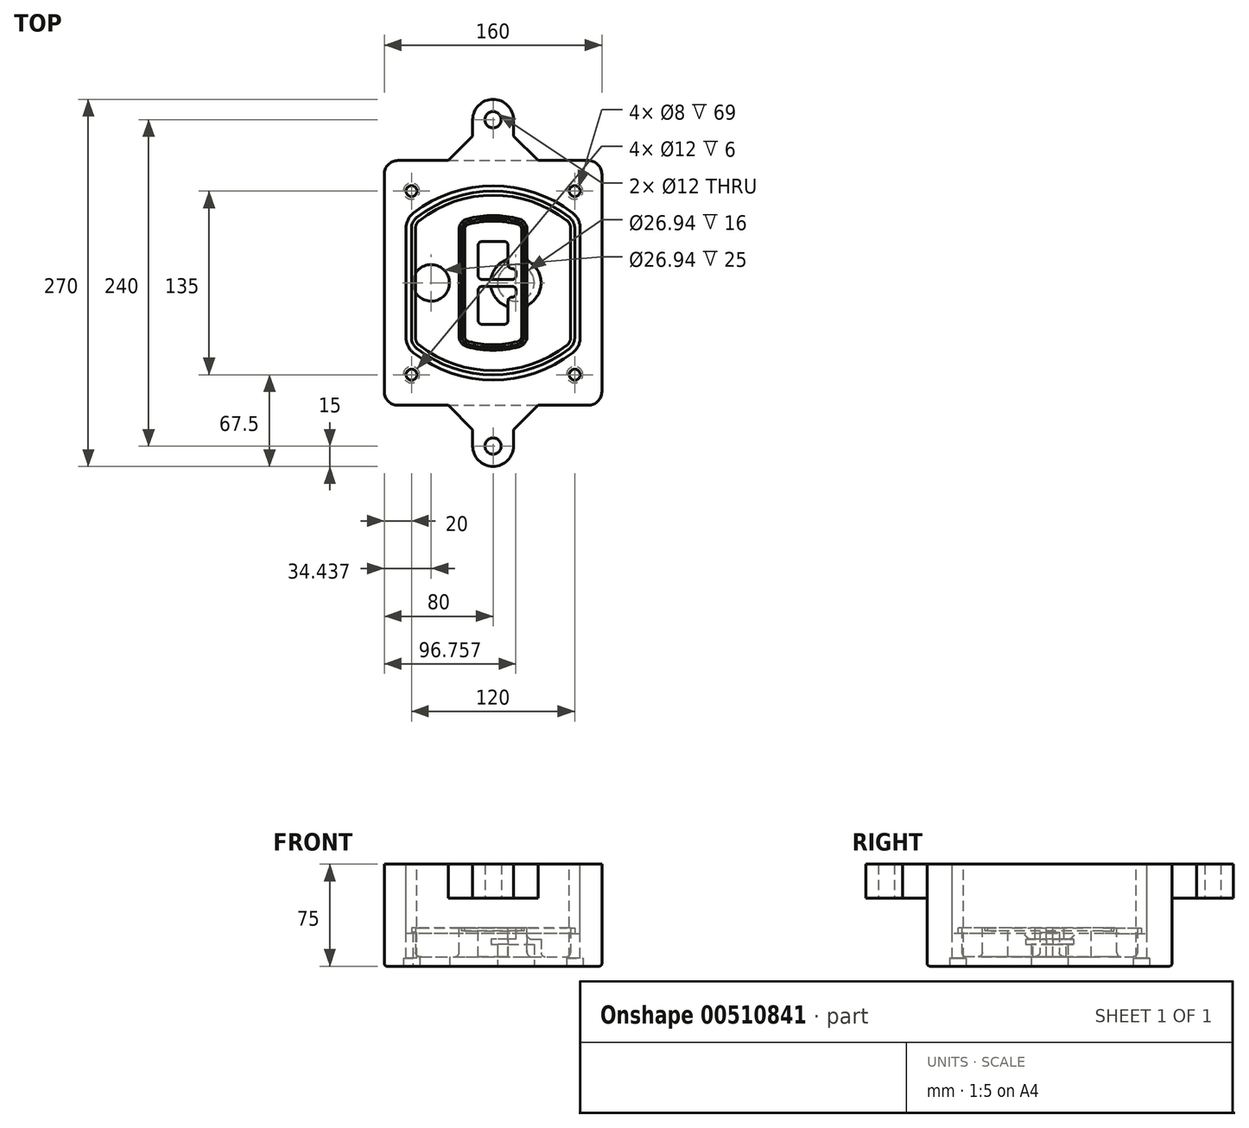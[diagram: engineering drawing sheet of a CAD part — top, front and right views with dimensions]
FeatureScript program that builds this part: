
annotation { "Feature Type Name" : "Feature", "Feature Type Description" : "" }
export const myFeature = defineFeature(function(context is Context, id is Id, definition is map)
    precondition{}
    {
        {
            var Q0;
            Q0=qCreatedBy(makeId("Top.planeOp"),FACE);
            var sketch = newSketch(context, id + "F0", { "sketchPlane" : qUnion([Q0])});
            skPoint(sketch, "E0.rect.middle", {"position": v(0, 0) * mm});
            skLineSegment(sketch, "E1.bottom", {"start": v(-70, -90) * mm, "end": v(70, -90) * mm});
            skLineSegment(sketch, "E1.top", {"start": v(-70, 90) * mm, "end": v(70, 90) * mm});
            skLineSegment(sketch, "E1.left", {"start": v(-80, -80) * mm, "end": v(-80, 80) * mm});
            skLineSegment(sketch, "E1.right", {"start": v(80, -80) * mm, "end": v(80, 80) * mm});
            skLineSegment(sketch, "E2", {"start": v(-80, 90) * mm, "end": v(80, -90) * mm, "construction": true});
            skLineSegment(sketch, "E3", {"start": v(80, 90) * mm, "end": v(-80, -90) * mm, "construction": true});
            skCircle(sketch, "E4", {"center": v(-60, 67.5) * mm, "radius": 4 * mm});
            skCircle(sketch, "E5", {"center": v(60, 67.5) * mm, "radius": 4 * mm});
            skCircle(sketch, "E6", {"center": v(60, -67.5) * mm, "radius": 4 * mm});
            skCircle(sketch, "E7", {"center": v(-60, -67.5) * mm, "radius": 4 * mm});
            skLineSegment(sketch, "E8", {"start": v(-60, 67.5) * mm, "end": v(60, 67.5) * mm, "construction": true});
            skLineSegment(sketch, "E9", {"start": v(60, 67.5) * mm, "end": v(60, -67.5) * mm, "construction": true});
            skLineSegment(sketch, "E10", {"start": v(60, -67.5) * mm, "end": v(-60, -67.5) * mm, "construction": true});
            skLineSegment(sketch, "E11", {"start": v(-60, -67.5) * mm, "end": v(-60, 67.5) * mm, "construction": true});
            skLineSegment(sketch, "E12", {"start": v(-60, 40.3) * mm, "end": v(-60, -40.3) * mm});
            skLineSegment(sketch, "E13", {"start": v(60, 40.3) * mm, "end": v(60, -40.3) * mm});
            skArc(sketch, "E14", {"start": v(56.15, 48.18) * mm, "mid": v(0, 67.5) * mm, "end": v(-56.15, 48.18) * mm});
            skArc(sketch, "E15", {"start": v(-56.15, -48.18) * mm, "mid": v(0, -67.5) * mm, "end": v(56.15, -48.18) * mm});
            skLineSegment(sketch, "E16", {"start": v(-60, 0) * mm, "end": v(60, 0) * mm, "construction": true});
            skPoint(sketch, "E17.visualSharp", {"position": v(-60, -45) * mm});
            skArc(sketch, "E17.filletArc", {"start": v(-60, -40.3) * mm, "mid": v(-58.99, -44.68) * mm, "end": v(-56.15, -48.18) * mm});
            skPoint(sketch, "E18.visualSharp", {"position": v(-60, 45) * mm});
            skArc(sketch, "E18.filletArc", {"start": v(-56.15, 48.18) * mm, "mid": v(-58.99, 44.68) * mm, "end": v(-60, 40.3) * mm});
            skPoint(sketch, "E19.visualSharp", {"position": v(60, 45) * mm});
            skArc(sketch, "E19.filletArc", {"start": v(60, 40.3) * mm, "mid": v(58.99, 44.68) * mm, "end": v(56.15, 48.18) * mm});
            skPoint(sketch, "E20.visualSharp", {"position": v(60, -45) * mm});
            skArc(sketch, "E20.filletArc", {"start": v(56.15, -48.18) * mm, "mid": v(58.99, -44.68) * mm, "end": v(60, -40.3) * mm});
            skPoint(sketch, "E21.visualSharp", {"position": v(-80, 90) * mm});
            skArc(sketch, "E21.filletArc", {"start": v(-70, 90) * mm, "mid": v(-77.07, 87.07) * mm, "end": v(-80, 80) * mm});
            skPoint(sketch, "E22.visualSharp", {"position": v(80, 90) * mm});
            skArc(sketch, "E22.filletArc", {"start": v(80, 80) * mm, "mid": v(77.07, 87.07) * mm, "end": v(70, 90) * mm});
            skPoint(sketch, "E23.visualSharp", {"position": v(80, -90) * mm});
            skArc(sketch, "E23.filletArc", {"start": v(70, -90) * mm, "mid": v(77.07, -87.07) * mm, "end": v(80, -80) * mm});
            skPoint(sketch, "E24.visualSharp", {"position": v(-80, -90) * mm});
            skArc(sketch, "E24.filletArc", {"start": v(-80, -80) * mm, "mid": v(-77.07, -87.07) * mm, "end": v(-70, -90) * mm});
            skArc(sketch, "E25.0", {"start": v(57, 40.3) * mm, "mid": v(56.3, 43.36) * mm, "end": v(54.3, 45.81) * mm});
            skLineSegment(sketch, "E25.1", {"start": v(57, 40.3) * mm, "end": v(57, -40.3) * mm});
            skArc(sketch, "E25.2", {"start": v(54.3, -45.81) * mm, "mid": v(56.3, -43.36) * mm, "end": v(57, -40.3) * mm});
            skArc(sketch, "E25.3", {"start": v(-54.3, -45.81) * mm, "mid": v(0, -64.5) * mm, "end": v(54.3, -45.81) * mm});
            skArc(sketch, "E25.4", {"start": v(-57, -40.3) * mm, "mid": v(-56.3, -43.36) * mm, "end": v(-54.3, -45.81) * mm});
            skArc(sketch, "E25.5", {"start": v(54.3, 45.81) * mm, "mid": v(0, 64.5) * mm, "end": v(-54.3, 45.81) * mm});
            skLineSegment(sketch, "E25.6", {"start": v(-57, 40.3) * mm, "end": v(-57, -40.3) * mm});
            skArc(sketch, "E25.7", {"start": v(-54.3, 45.81) * mm, "mid": v(-56.3, 43.36) * mm, "end": v(-57, 40.3) * mm});
            skArc(sketch, "E26.0", {"start": v(-58.62, 51.33) * mm, "mid": v(-62.58, 46.43) * mm, "end": v(-64, 40.3) * mm});
            skArc(sketch, "E26.1", {"start": v(58.62, 51.33) * mm, "mid": v(0, 71.5) * mm, "end": v(-58.62, 51.33) * mm});
            skArc(sketch, "E26.2", {"start": v(64, 40.3) * mm, "mid": v(62.58, 46.43) * mm, "end": v(58.62, 51.33) * mm});
            skLineSegment(sketch, "E26.3", {"start": v(64, 40.3) * mm, "end": v(64, -40.3) * mm});
            skArc(sketch, "E26.4", {"start": v(58.62, -51.33) * mm, "mid": v(62.58, -46.43) * mm, "end": v(64, -40.3) * mm});
            skLineSegment(sketch, "E26.5", {"start": v(-64, 40.3) * mm, "end": v(-64, -40.3) * mm});
            skArc(sketch, "E26.6", {"start": v(-58.62, -51.33) * mm, "mid": v(0, -71.5) * mm, "end": v(58.62, -51.33) * mm});
            skArc(sketch, "E26.7", {"start": v(-64, -40.3) * mm, "mid": v(-62.58, -46.43) * mm, "end": v(-58.62, -51.33) * mm});
            skSolve(sketch);
        }
        {
            var Q0;
            Q0=makeQuery(id+"F0.imprint","IMPRINT",FACE,{"disambiguationData":[TD([[makeQuery(id+"F0.imprint","IMPRINT",EDGE,{"derivedFrom":sQuery(id+"F0.wireOp",EDGE,"E1.bottom")}),1.0]])]});
            var Q1;
            Q1=makeQuery(id+"F0.imprint","IMPRINT",FACE,{"disambiguationData":[TD([[makeQuery(id+"F0.imprint","IMPRINT",EDGE,{"derivedFrom":sQuery(id+"F0.wireOp",EDGE,"E12")}),1.0]])]});
            var Q2;
            Q2=makeQuery(id+"F0.imprint","IMPRINT",FACE,{"disambiguationData":[TD([[makeQuery(id+"F0.imprint","IMPRINT",EDGE,{"derivedFrom":sQuery(id+"F0.wireOp",EDGE,"E25.0")}),1.0]])]});
            var Q3;
            Q3=makeQuery(id+"F0.imprint","IMPRINT",FACE,{"disambiguationData":[TD([[makeQuery(id+"F0.imprint","IMPRINT",EDGE,{"derivedFrom":sQuery(id+"F0.wireOp",EDGE,"E12")}),-1.0]])]});
            extrude(context, id + "F1", {"entities" : qUnion([Q0, Q1, Q2, Q3]), "oppositeDirection" : true, "depth" : 25 * mm});
        }
        {
            var Q0;
            Q0=makeQuery(id+"F0.imprint","IMPRINT",FACE,{"disambiguationData":[TD([[makeQuery(id+"F0.imprint","IMPRINT",EDGE,{"derivedFrom":sQuery(id+"F0.wireOp",EDGE,"E12")}),1.0]])]});
            extrude(context, id + "F2", {"entities" : qUnion([Q0]), "operationType" : NewBodyOperationType.ADD, "depth" : 3 * mm});
        }
        {
            var Q0;
            Q0=makeQuery(id+"F0.imprint","IMPRINT",FACE,{"disambiguationData":[TD([[makeQuery(id+"F0.imprint","IMPRINT",EDGE,{"derivedFrom":sQuery(id+"F0.wireOp",EDGE,"E12")}),-1.0]])]});
            extrude(context, id + "F3", {"entities" : qUnion([Q0]), "operationType" : NewBodyOperationType.REMOVE, "oppositeDirection" : true, "depth" : 1 * mm});
        }
        {
            var Q0;
            Q0=makeQuery(id+"F0.imprint","IMPRINT",FACE,{"disambiguationData":[TD([[makeQuery(id+"F0.imprint","IMPRINT",EDGE,{"derivedFrom":sQuery(id+"F0.wireOp",EDGE,"E25.0")}),1.0]])]});
            extrude(context, id + "F4", {"entities" : qUnion([Q0]), "operationType" : NewBodyOperationType.REMOVE, "oppositeDirection" : true, "depth" : 18 * mm});
        }
        {
            var Q0;
            Q0=makeQuery(id+"F2.opExtrude","CAP_FACE",FACE,{"disambiguationData":[OSD([sQuery(id+"F0.wireOp",EDGE,"E12"),sQuery(id+"F0.wireOp",EDGE,"E13"),sQuery(id+"F0.wireOp",EDGE,"E14"),sQuery(id+"F0.wireOp",EDGE,"E15"),sQuery(id+"F0.wireOp",EDGE,"E17.filletArc"),sQuery(id+"F0.wireOp",EDGE,"E18.filletArc"),sQuery(id+"F0.wireOp",EDGE,"E19.filletArc"),sQuery(id+"F0.wireOp",EDGE,"E20.filletArc"),sQuery(id+"F0.wireOp",EDGE,"E25.0"),sQuery(id+"F0.wireOp",EDGE,"E25.1"),sQuery(id+"F0.wireOp",EDGE,"E25.2"),sQuery(id+"F0.wireOp",EDGE,"E25.3"),sQuery(id+"F0.wireOp",EDGE,"E25.4"),sQuery(id+"F0.wireOp",EDGE,"E25.5"),sQuery(id+"F0.wireOp",EDGE,"E25.6"),sQuery(id+"F0.wireOp",EDGE,"E25.7")])],"isStart":false});
            var sketch = newSketch(context, id + "F5", { "sketchPlane" : qUnion([Q0])});
            skArc(sketch, "E27.0", {"start": v(-19.08, -46.97) * mm, "mid": v(0, -49.5) * mm, "end": v(19.08, -46.97) * mm});
            skArc(sketch, "E28.0", {"start": v(19.08, 46.97) * mm, "mid": v(0, 49.5) * mm, "end": v(-19.08, 46.97) * mm});
            skLineSegment(sketch, "E29", {"start": v(-25, 39.25) * mm, "end": v(-25, -39.25) * mm});
            skLineSegment(sketch, "E30", {"start": v(25, 39.25) * mm, "end": v(25, -39.25) * mm});
            skLineSegment(sketch, "E31", {"start": v(-25, 45.1) * mm, "end": v(25, 45.1) * mm, "construction": true});
            skLineSegment(sketch, "E32", {"start": v(-25, -45.1) * mm, "end": v(25, -45.1) * mm, "construction": true});
            skPoint(sketch, "E33.visualSharp", {"position": v(-25, 45.1) * mm});
            skArc(sketch, "E33.filletArc", {"start": v(-19.08, 46.97) * mm, "mid": v(-23.35, 44.11) * mm, "end": v(-25, 39.25) * mm});
            skPoint(sketch, "E34.visualSharp", {"position": v(25, 45.1) * mm});
            skArc(sketch, "E34.filletArc", {"start": v(25, 39.25) * mm, "mid": v(23.35, 44.11) * mm, "end": v(19.08, 46.97) * mm});
            skPoint(sketch, "E35.visualSharp", {"position": v(25, -45.1) * mm});
            skArc(sketch, "E35.filletArc", {"start": v(19.08, -46.97) * mm, "mid": v(23.35, -44.11) * mm, "end": v(25, -39.25) * mm});
            skPoint(sketch, "E36.visualSharp", {"position": v(-25, -45.1) * mm});
            skArc(sketch, "E36.filletArc", {"start": v(-25, -39.25) * mm, "mid": v(-23.35, -44.11) * mm, "end": v(-19.08, -46.97) * mm});
            skArc(sketch, "E37.0", {"start": v(54.3, 45.81) * mm, "mid": v(0, 64.5) * mm, "end": v(-54.3, 45.81) * mm});
            skArc(sketch, "E37.1", {"start": v(-54.3, 45.81) * mm, "mid": v(-56.3, 43.36) * mm, "end": v(-57, 40.3) * mm});
            skLineSegment(sketch, "E37.2", {"start": v(-57, 40.3) * mm, "end": v(-57, -40.3) * mm});
            skArc(sketch, "E37.3", {"start": v(-57, -40.3) * mm, "mid": v(-56.3, -43.36) * mm, "end": v(-54.3, -45.81) * mm});
            skArc(sketch, "E37.4", {"start": v(-54.3, -45.81) * mm, "mid": v(0, -64.5) * mm, "end": v(54.3, -45.81) * mm});
            skArc(sketch, "E37.5", {"start": v(54.3, -45.81) * mm, "mid": v(56.3, -43.36) * mm, "end": v(57, -40.3) * mm});
            skLineSegment(sketch, "E37.6", {"start": v(57, 40.3) * mm, "end": v(57, -40.3) * mm});
            skArc(sketch, "E37.7", {"start": v(57, 40.3) * mm, "mid": v(56.3, 43.36) * mm, "end": v(54.3, 45.81) * mm});
            skLineSegment(sketch, "E38.0", {"start": v(23, 39.25) * mm, "end": v(23, -39.25) * mm});
            skArc(sketch, "E38.1", {"start": v(18.56, -45.04) * mm, "mid": v(21.76, -42.9) * mm, "end": v(23, -39.25) * mm});
            skArc(sketch, "E38.2", {"start": v(-18.56, -45.04) * mm, "mid": v(0, -47.5) * mm, "end": v(18.56, -45.04) * mm});
            skArc(sketch, "E38.3", {"start": v(-23, -39.25) * mm, "mid": v(-21.76, -42.9) * mm, "end": v(-18.56, -45.04) * mm});
            skLineSegment(sketch, "E38.4", {"start": v(-23, 39.25) * mm, "end": v(-23, -39.25) * mm});
            skArc(sketch, "E38.5", {"start": v(23, 39.25) * mm, "mid": v(21.76, 42.9) * mm, "end": v(18.56, 45.04) * mm});
            skArc(sketch, "E38.6", {"start": v(-18.56, 45.04) * mm, "mid": v(-21.76, 42.9) * mm, "end": v(-23, 39.25) * mm});
            skArc(sketch, "E38.7", {"start": v(18.56, 45.04) * mm, "mid": v(0, 47.5) * mm, "end": v(-18.56, 45.04) * mm});
            skArc(sketch, "E39.0", {"start": v(21, 39.25) * mm, "mid": v(20.18, 41.68) * mm, "end": v(18.04, 43.1) * mm});
            skLineSegment(sketch, "E39.1", {"start": v(21, 39.25) * mm, "end": v(21, -39.25) * mm});
            skArc(sketch, "E39.2", {"start": v(18.04, -43.1) * mm, "mid": v(20.18, -41.68) * mm, "end": v(21, -39.25) * mm});
            skArc(sketch, "E39.3", {"start": v(-18.04, -43.1) * mm, "mid": v(0, -45.5) * mm, "end": v(18.04, -43.1) * mm});
            skArc(sketch, "E39.4", {"start": v(-21, -39.25) * mm, "mid": v(-20.18, -41.68) * mm, "end": v(-18.04, -43.1) * mm});
            skArc(sketch, "E39.5", {"start": v(18.04, 43.1) * mm, "mid": v(0, 45.5) * mm, "end": v(-18.04, 43.1) * mm});
            skLineSegment(sketch, "E39.6", {"start": v(-21, 39.25) * mm, "end": v(-21, -39.25) * mm});
            skArc(sketch, "E39.7", {"start": v(-18.04, 43.1) * mm, "mid": v(-20.18, 41.68) * mm, "end": v(-21, 39.25) * mm});
            skLineSegment(sketch, "E40", {"start": v(-25, 0) * mm, "end": v(25, 0) * mm, "construction": true});
            skLineSegment(sketch, "E41", {"start": v(-11, 5.5) * mm, "end": v(-11, 27.5) * mm});
            skLineSegment(sketch, "E42", {"start": v(-8, 30.5) * mm, "end": v(8, 30.5) * mm});
            skLineSegment(sketch, "E43", {"start": v(11, 27.5) * mm, "end": v(11, 13.5) * mm});
            skLineSegment(sketch, "E44", {"start": v(14, 10.5) * mm, "end": v(14, 10.5) * mm});
            skLineSegment(sketch, "E45", {"start": v(17, 7.5) * mm, "end": v(17, 5.5) * mm});
            skLineSegment(sketch, "E46", {"start": v(14, 2.5) * mm, "end": v(-8, 2.5) * mm});
            skPoint(sketch, "E47.visualSharp", {"position": v(-11, 30.5) * mm});
            skArc(sketch, "E47.filletArc", {"start": v(-8, 30.5) * mm, "mid": v(-10.12, 29.62) * mm, "end": v(-11, 27.5) * mm});
            skPoint(sketch, "E48.visualSharp", {"position": v(11, 30.5) * mm});
            skArc(sketch, "E48.filletArc", {"start": v(11, 27.5) * mm, "mid": v(10.12, 29.62) * mm, "end": v(8, 30.5) * mm});
            skPoint(sketch, "E49.visualSharp", {"position": v(11, 10.5) * mm});
            skArc(sketch, "E49.filletArc", {"start": v(11, 13.5) * mm, "mid": v(11.88, 11.38) * mm, "end": v(14, 10.5) * mm});
            skPoint(sketch, "E50.visualSharp", {"position": v(17, 10.5) * mm});
            skArc(sketch, "E50.filletArc", {"start": v(17, 7.5) * mm, "mid": v(16.12, 9.62) * mm, "end": v(14, 10.5) * mm});
            skPoint(sketch, "E51.visualSharp", {"position": v(17, 2.5) * mm});
            skArc(sketch, "E51.filletArc", {"start": v(14, 2.5) * mm, "mid": v(16.12, 3.38) * mm, "end": v(17, 5.5) * mm});
            skPoint(sketch, "E52.visualSharp", {"position": v(-11, 2.5) * mm});
            skArc(sketch, "E52.filletArc", {"start": v(-11, 5.5) * mm, "mid": v(-10.12, 3.38) * mm, "end": v(-8, 2.5) * mm});
            skLineSegment(sketch, "E53.0.MirrorCS", {"start": v(14, -2.5) * mm, "end": v(-8, -2.5) * mm});
            skArc(sketch, "E54.0.MirrorCS", {"start": v(-11, -5.5) * mm, "mid": v(-10.12, -3.38) * mm, "end": v(-8, -2.5) * mm});
            skLineSegment(sketch, "E55.0.MirrorCS", {"start": v(-11, -5.5) * mm, "end": v(-11, -27.5) * mm});
            skArc(sketch, "E56.0.MirrorCS", {"start": v(-8, -30.5) * mm, "mid": v(-10.12, -29.62) * mm, "end": v(-11, -27.5) * mm});
            skLineSegment(sketch, "E57.0.MirrorCS", {"start": v(-8, -30.5) * mm, "end": v(8, -30.5) * mm});
            skArc(sketch, "E58.0.MirrorCS", {"start": v(11, -27.5) * mm, "mid": v(10.12, -29.62) * mm, "end": v(8, -30.5) * mm});
            skLineSegment(sketch, "E59.0.MirrorCS", {"start": v(11, -27.5) * mm, "end": v(11, -13.5) * mm});
            skArc(sketch, "E60.0.MirrorCS", {"start": v(11, -13.5) * mm, "mid": v(11.88, -11.38) * mm, "end": v(14, -10.5) * mm});
            skArc(sketch, "E61.0.MirrorCS", {"start": v(17, -7.5) * mm, "mid": v(16.12, -9.62) * mm, "end": v(14, -10.5) * mm});
            skLineSegment(sketch, "E62.0.MirrorCS", {"start": v(17, -7.5) * mm, "end": v(17, -5.5) * mm});
            skArc(sketch, "E63.0.MirrorCS", {"start": v(14, -2.5) * mm, "mid": v(16.12, -3.38) * mm, "end": v(17, -5.5) * mm});
            skSolve(sketch);
        }
        {
            var Q0;
            Q0=makeQuery(id+"F5.imprint","IMPRINT",FACE,{"disambiguationData":[TD([[makeQuery(id+"F5.imprint","IMPRINT",EDGE,{"derivedFrom":sQuery(id+"F5.wireOp",EDGE,"E27.0")}),1.0]])]});
            var Q1;
            Q1=makeQuery(id+"F5.imprint","IMPRINT",FACE,{"disambiguationData":[TD([[makeQuery(id+"F5.imprint","IMPRINT",EDGE,{"derivedFrom":sQuery(id+"F5.wireOp",EDGE,"E38.0")}),-1.0]])]});
            var Q2;
            Q2=makeQuery(id+"F5.imprint","IMPRINT",FACE,{"disambiguationData":[TD([[makeQuery(id+"F5.imprint","IMPRINT",EDGE,{"derivedFrom":sQuery(id+"F5.wireOp",EDGE,"E39.0")}),1.0]])]});
            extrude(context, id + "F6", {"entities" : qUnion([Q0, Q1, Q2]), "operationType" : NewBodyOperationType.ADD, "endBound" : BoundingType.UP_TO_NEXT, "oppositeDirection" : true, "depth" : 25 * mm});
        }
        {
            var Q0;
            Q0=makeQuery(id+"F5.imprint","IMPRINT",FACE,{"disambiguationData":[TD([[makeQuery(id+"F5.imprint","IMPRINT",EDGE,{"derivedFrom":sQuery(id+"F5.wireOp",EDGE,"E38.0")}),-1.0]])]});
            extrude(context, id + "F7", {"entities" : qUnion([Q0]), "operationType" : NewBodyOperationType.REMOVE, "oppositeDirection" : true, "depth" : 2 * mm});
        }
        {
            var Q0;
            Q0=makeQuery(id+"F1.opExtrude","CAP_FACE",FACE,{"disambiguationData":[OSD([sQuery(id+"F0.wireOp",EDGE,"E1.bottom"),sQuery(id+"F0.wireOp",EDGE,"E1.top"),sQuery(id+"F0.wireOp",EDGE,"E1.left"),sQuery(id+"F0.wireOp",EDGE,"E1.right"),sQuery(id+"F0.wireOp",EDGE,"E4"),sQuery(id+"F0.wireOp",EDGE,"E5"),sQuery(id+"F0.wireOp",EDGE,"E6"),sQuery(id+"F0.wireOp",EDGE,"E7"),sQuery(id+"F0.wireOp",EDGE,"E21.filletArc"),sQuery(id+"F0.wireOp",EDGE,"E22.filletArc"),sQuery(id+"F0.wireOp",EDGE,"E23.filletArc"),sQuery(id+"F0.wireOp",EDGE,"E24.filletArc")])],"isStart":false});
            var sketch = newSketch(context, id + "F8", { "sketchPlane" : qUnion([Q0])});
            skCircle(sketch, "E64", {"center": v(16.76, 0) * mm, "radius": 13.47 * mm});
            skCircle(sketch, "E65", {"center": v(-45.56, 0) * mm, "radius": 13.47 * mm});
            skLineSegment(sketch, "E66", {"start": v(80, 0) * mm, "end": v(-80, 0) * mm});
            skCircle(sketch, "E67", {"center": v(16.76, 0) * mm, "radius": 18.47 * mm});
            skCircle(sketch, "E68", {"center": v(60, -67.5) * mm, "radius": 6 * mm});
            skCircle(sketch, "E69", {"center": v(-60, -67.5) * mm, "radius": 6 * mm});
            skCircle(sketch, "E70", {"center": v(-60, 67.5) * mm, "radius": 6 * mm});
            skCircle(sketch, "E71", {"center": v(60, 67.5) * mm, "radius": 6 * mm});
            skSolve(sketch);
        }
        {
            var Q0;
            {var subQ1=sQuery(id+"F8.wireOp",EDGE,"E66");var subQ4=sQuery(id+"F8.wireOp",EDGE,"E64");var subQ6=makeQuery(id+"F8.imprint","INTERSECT",VERTEX,{"disambiguationData":[OD(0.0)],"derivedFrom":[subQ4,subQ1]});Q0=makeQuery(id+"F8.imprint","IMPRINT",FACE,{"disambiguationData":[TD([[makeQuery(id+"F8.imprint","IMPRINT",EDGE,{"disambiguationData":[TD([[subQ6,-1.0]])],"derivedFrom":subQ4}),-1.0]])]});}
            var Q1;
            {var subQ0=sQuery(id+"F8.wireOp",EDGE,"E66");var subQ1=sQuery(id+"F8.wireOp",EDGE,"E64");var subQ3=makeQuery(id+"F8.imprint","INTERSECT",VERTEX,{"disambiguationData":[OD(0.0)],"derivedFrom":[subQ1,subQ0]});Q1=makeQuery(id+"F8.imprint","IMPRINT",FACE,{"disambiguationData":[TD([[makeQuery(id+"F8.imprint","IMPRINT",EDGE,{"disambiguationData":[TD([[subQ3,-1.0]])],"derivedFrom":subQ1}),1.0]])]});}
            var Q2;
            {var subQ0=sQuery(id+"F8.wireOp",EDGE,"E66");var subQ1=sQuery(id+"F8.wireOp",EDGE,"E64");var subQ3=makeQuery(id+"F8.imprint","INTERSECT",VERTEX,{"disambiguationData":[OD(0.0)],"derivedFrom":[subQ1,subQ0]});Q2=makeQuery(id+"F8.imprint","IMPRINT",FACE,{"disambiguationData":[TD([[makeQuery(id+"F8.imprint","IMPRINT",EDGE,{"disambiguationData":[TD([[subQ3,1.0]])],"derivedFrom":subQ1}),1.0]])]});}
            var Q3;
            {var subQ1=sQuery(id+"F8.wireOp",EDGE,"E66");var subQ4=sQuery(id+"F8.wireOp",EDGE,"E64");var subQ6=makeQuery(id+"F8.imprint","INTERSECT",VERTEX,{"disambiguationData":[OD(0.0)],"derivedFrom":[subQ4,subQ1]});Q3=makeQuery(id+"F8.imprint","IMPRINT",FACE,{"disambiguationData":[TD([[makeQuery(id+"F8.imprint","IMPRINT",EDGE,{"disambiguationData":[TD([[subQ6,1.0]])],"derivedFrom":subQ4}),-1.0]])]});}
            extrude(context, id + "F9", {"entities" : qUnion([Q0, Q1, Q2, Q3]), "operationType" : NewBodyOperationType.ADD, "oppositeDirection" : true, "depth" : 20 * mm});
        }
        {
            var Q0;
            {var subQ0=sQuery(id+"F8.wireOp",EDGE,"E66");var subQ1=sQuery(id+"F8.wireOp",EDGE,"E64");var subQ3=makeQuery(id+"F8.imprint","INTERSECT",VERTEX,{"disambiguationData":[OD(0.0)],"derivedFrom":[subQ1,subQ0]});Q0=makeQuery(id+"F8.imprint","IMPRINT",FACE,{"disambiguationData":[TD([[makeQuery(id+"F8.imprint","IMPRINT",EDGE,{"disambiguationData":[TD([[subQ3,-1.0]])],"derivedFrom":subQ1}),1.0]])]});}
            var Q1;
            {var subQ0=sQuery(id+"F8.wireOp",EDGE,"E66");var subQ1=sQuery(id+"F8.wireOp",EDGE,"E64");var subQ3=makeQuery(id+"F8.imprint","INTERSECT",VERTEX,{"disambiguationData":[OD(0.0)],"derivedFrom":[subQ1,subQ0]});Q1=makeQuery(id+"F8.imprint","IMPRINT",FACE,{"disambiguationData":[TD([[makeQuery(id+"F8.imprint","IMPRINT",EDGE,{"disambiguationData":[TD([[subQ3,1.0]])],"derivedFrom":subQ1}),1.0]])]});}
            extrude(context, id + "F10", {"entities" : qUnion([Q0, Q1]), "operationType" : NewBodyOperationType.REMOVE, "oppositeDirection" : true, "depth" : 16 * mm});
        }
        {
            var Q0;
            {var subQ0=sQuery(id+"F8.wireOp",EDGE,"E66");var subQ1=sQuery(id+"F8.wireOp",EDGE,"E65");var subQ3=makeQuery(id+"F8.imprint","INTERSECT",VERTEX,{"disambiguationData":[OD(0.0)],"derivedFrom":[subQ1,subQ0]});Q0=makeQuery(id+"F8.imprint","IMPRINT",FACE,{"disambiguationData":[TD([[makeQuery(id+"F8.imprint","IMPRINT",EDGE,{"disambiguationData":[TD([[subQ3,-1.0]])],"derivedFrom":subQ1}),1.0]])]});}
            var Q1;
            {var subQ0=sQuery(id+"F8.wireOp",EDGE,"E66");var subQ1=sQuery(id+"F8.wireOp",EDGE,"E65");var subQ3=makeQuery(id+"F8.imprint","INTERSECT",VERTEX,{"disambiguationData":[OD(0.0)],"derivedFrom":[subQ1,subQ0]});Q1=makeQuery(id+"F8.imprint","IMPRINT",FACE,{"disambiguationData":[TD([[makeQuery(id+"F8.imprint","IMPRINT",EDGE,{"disambiguationData":[TD([[subQ3,1.0]])],"derivedFrom":subQ1}),1.0]])]});}
            extrude(context, id + "F11", {"entities" : qUnion([Q0, Q1]), "operationType" : NewBodyOperationType.REMOVE, "oppositeDirection" : true, "depth" : 25 * mm});
        }
        {
            var Q0;
            Q0=makeQuery(id+"F8.imprint","IMPRINT",FACE,{"disambiguationData":[TD([[makeQuery(id+"F8.imprint","IMPRINT",EDGE,{"derivedFrom":sQuery(id+"F8.wireOp",EDGE,"E68")}),1.0]])]});
            var Q1;
            Q1=makeQuery(id+"F8.imprint","IMPRINT",FACE,{"disambiguationData":[TD([[makeQuery(id+"F8.imprint","IMPRINT",EDGE,{"derivedFrom":makeQuery(id+"F1.opExtrude","CAP_EDGE",EDGE,{"disambiguationData":[OSD([sQuery(id+"F0.wireOp",EDGE,"E5")])],"isStart":false})}),-1.0]])]});
            var Q2;
            Q2=makeQuery(id+"F8.imprint","IMPRINT",FACE,{"disambiguationData":[TD([[makeQuery(id+"F8.imprint","IMPRINT",EDGE,{"derivedFrom":sQuery(id+"F8.wireOp",EDGE,"E69")}),1.0]])]});
            var Q3;
            Q3=makeQuery(id+"F8.imprint","IMPRINT",FACE,{"disambiguationData":[TD([[makeQuery(id+"F8.imprint","IMPRINT",EDGE,{"derivedFrom":makeQuery(id+"F1.opExtrude","CAP_EDGE",EDGE,{"disambiguationData":[OSD([sQuery(id+"F0.wireOp",EDGE,"E4")])],"isStart":false})}),-1.0]])]});
            var Q4;
            Q4=makeQuery(id+"F8.imprint","IMPRINT",FACE,{"disambiguationData":[TD([[makeQuery(id+"F8.imprint","IMPRINT",EDGE,{"derivedFrom":sQuery(id+"F8.wireOp",EDGE,"E70")}),1.0]])]});
            var Q5;
            Q5=makeQuery(id+"F8.imprint","IMPRINT",FACE,{"disambiguationData":[TD([[makeQuery(id+"F8.imprint","IMPRINT",EDGE,{"derivedFrom":makeQuery(id+"F1.opExtrude","CAP_EDGE",EDGE,{"disambiguationData":[OSD([sQuery(id+"F0.wireOp",EDGE,"E7")])],"isStart":false})}),-1.0]])]});
            var Q6;
            Q6=makeQuery(id+"F8.imprint","IMPRINT",FACE,{"disambiguationData":[TD([[makeQuery(id+"F8.imprint","IMPRINT",EDGE,{"derivedFrom":sQuery(id+"F8.wireOp",EDGE,"E71")}),1.0]])]});
            var Q7;
            Q7=makeQuery(id+"F8.imprint","IMPRINT",FACE,{"disambiguationData":[TD([[makeQuery(id+"F8.imprint","IMPRINT",EDGE,{"derivedFrom":makeQuery(id+"F1.opExtrude","CAP_EDGE",EDGE,{"disambiguationData":[OSD([sQuery(id+"F0.wireOp",EDGE,"E6")])],"isStart":false})}),-1.0]])]});
            extrude(context, id + "F12", {"entities" : qUnion([Q0, Q1, Q2, Q3, Q4, Q5, Q6, Q7]), "operationType" : NewBodyOperationType.REMOVE, "oppositeDirection" : true, "depth" : 6 * mm});
        }
        {
            var Q0;
            Q0=makeQuery(id+"F10.boolean.opBoolean","COPY",FACE,{"derivedFrom":makeQuery(id+"F10.opExtrude","CAP_FACE",FACE,{"disambiguationData":[OSD([sQuery(id+"F8.wireOp",EDGE,"E64")])],"isStart":false})});
            var sketch = newSketch(context, id + "F13", { "sketchPlane" : qUnion([Q0])});
            skArc(sketch, "E72.0", {"start": v(11, 17.55) * mm, "mid": v(2.57, 11.82) * mm, "end": v(-1.54, 2.5) * mm});
            skArc(sketch, "E72.1", {"start": v(-1.54, -2.5) * mm, "mid": v(2.57, -11.82) * mm, "end": v(11, -17.55) * mm});
            skLineSegment(sketch, "E73", {"start": v(-1.54, -2.5) * mm, "end": v(14, -2.5) * mm});
            skLineSegment(sketch, "E74.0", {"start": v(14, 2.5) * mm, "end": v(-1.54, 2.5) * mm});
            skArc(sketch, "E74.1", {"start": v(14, 2.5) * mm, "mid": v(16.12, 3.38) * mm, "end": v(17, 5.5) * mm});
            skLineSegment(sketch, "E74.2", {"start": v(17, 7.5) * mm, "end": v(17, 5.5) * mm});
            skArc(sketch, "E74.3", {"start": v(17, 7.5) * mm, "mid": v(16.12, 9.62) * mm, "end": v(14, 10.5) * mm});
            skArc(sketch, "E74.4", {"start": v(11, 13.5) * mm, "mid": v(11.88, 11.38) * mm, "end": v(14, 10.5) * mm});
            skLineSegment(sketch, "E74.5", {"start": v(11, 17.55) * mm, "end": v(11, 13.5) * mm});
            skLineSegment(sketch, "E74.7", {"start": v(14, -2.5) * mm, "end": v(-1.54, -2.5) * mm});
            skArc(sketch, "E74.8", {"start": v(14, -2.5) * mm, "mid": v(16.12, -3.38) * mm, "end": v(17, -5.5) * mm});
            skLineSegment(sketch, "E74.9", {"start": v(17, -7.5) * mm, "end": v(17, -5.5) * mm});
            skArc(sketch, "E74.10", {"start": v(17, -7.5) * mm, "mid": v(16.12, -9.62) * mm, "end": v(14, -10.5) * mm});
            skArc(sketch, "E74.11", {"start": v(11, -13.5) * mm, "mid": v(11.88, -11.38) * mm, "end": v(14, -10.5) * mm});
            skLineSegment(sketch, "E74.12", {"start": v(11, -17.55) * mm, "end": v(11, -13.5) * mm});
            skPoint(sketch, "E75.orphan", {"position": v(11, -27.5) * mm});
            skPoint(sketch, "E76.orphan", {"position": v(-8, -2.5) * mm});
            skPoint(sketch, "E77.orphan", {"position": v(-8, 2.5) * mm});
            skPoint(sketch, "E78.orphan", {"position": v(11, 27.5) * mm});
            skSolve(sketch);
        }
        {
            var Q0;
            {var subQ7=sQuery(id+"F13.wireOp",EDGE,"E72.0");var subQ14=sQuery(id+"F13.wireOp",EDGE,"E72.1");var subQ16=sQuery(id+"F13.wireOp",EDGE,"E74.1");var subQ18=sQuery(id+"F13.wireOp",EDGE,"E74.8");Q0=qUnion([makeQuery(id+"F13.imprint","IMPRINT",FACE,{"disambiguationData":[TD([[makeQuery(id+"F13.imprint","IMPRINT",EDGE,{"derivedFrom":subQ7}),1.0]])]}),makeQuery(id+"F13.imprint","IMPRINT",FACE,{"disambiguationData":[TD([[makeQuery(id+"F13.imprint","IMPRINT",EDGE,{"derivedFrom":subQ14}),1.0]])]}),makeQuery(id+"F13.imprint","IMPRINT",FACE,{"disambiguationData":[TD([[makeQuery(id+"F13.imprint","IMPRINT",EDGE,{"derivedFrom":subQ16}),1.0]])]}),makeQuery(id+"F13.imprint","IMPRINT",FACE,{"disambiguationData":[TD([[makeQuery(id+"F13.imprint","IMPRINT",EDGE,{"derivedFrom":subQ18}),-1.0]])]})]);}
            var Q1;
            Q1=makeQuery(id+"F6.boolean.opBoolean","SPLIT",FACE,{"disambiguationData":[TD([makeQuery(id+"F6.opExtrude","SWEPT_FACE",FACE,{"disambiguationData":[OSD([sQuery(id+"F5.wireOp",EDGE,"E41")])]})])],"derivedFrom":makeQuery(id+"F4.boolean.opBoolean","COPY",FACE,{"derivedFrom":makeQuery(id+"F4.opExtrude","CAP_FACE",FACE,{"disambiguationData":[OSD([sQuery(id+"F0.wireOp",EDGE,"E25.0"),sQuery(id+"F0.wireOp",EDGE,"E25.1"),sQuery(id+"F0.wireOp",EDGE,"E25.2"),sQuery(id+"F0.wireOp",EDGE,"E25.3"),sQuery(id+"F0.wireOp",EDGE,"E25.4"),sQuery(id+"F0.wireOp",EDGE,"E25.5"),sQuery(id+"F0.wireOp",EDGE,"E25.6"),sQuery(id+"F0.wireOp",EDGE,"E25.7")])],"isStart":false})})});
            extrude(context, id + "F14", {"entities" : qUnion([Q0]), "operationType" : NewBodyOperationType.REMOVE, "endBound" : BoundingType.UP_TO_SURFACE, "endBoundEntityFace" : qUnion([Q1]), "depth" : 25 * mm});
        }
        {
            var Q0;
            Q0=makeQuery(id+"F4.boolean.opBoolean","COPY",EDGE,{"derivedFrom":makeQuery(id+"F4.opExtrude","CAP_EDGE",EDGE,{"disambiguationData":[OSD([sQuery(id+"F0.wireOp",EDGE,"E25.6")])],"isStart":false})});
            var Q1;
            Q1=makeQuery(id+"F9.boolean.opBoolean","INTERSECT",EDGE,{"derivedFrom":[makeQuery(id+"F6.opExtrude","SWEPT_FACE",FACE,{"disambiguationData":[OSD([sQuery(id+"F5.wireOp",EDGE,"E30")])]}),makeQuery(id+"F9.opExtrude","CAP_FACE",FACE,{"disambiguationData":[OSD([sQuery(id+"F8.wireOp",EDGE,"E67")])],"isStart":false})]});
            var Q2;
            Q2=makeQuery(id+"F9.boolean.opBoolean","INTERSECT",EDGE,{"disambiguationData":[OD(1.0)],"derivedFrom":[makeQuery(id+"F6.opExtrude","SWEPT_FACE",FACE,{"disambiguationData":[OSD([sQuery(id+"F5.wireOp",EDGE,"E30")])]}),makeQuery(id+"F9.opExtrude","SWEPT_FACE",FACE,{"disambiguationData":[OSD([sQuery(id+"F8.wireOp",EDGE,"E67")])]})]});
            var Q3;
            {var subQ0=sQuery(id+"F5.wireOp",EDGE,"E30");Q3=makeQuery(id+"F9.boolean.opBoolean","SPLIT",EDGE,{"disambiguationData":[TD([makeQuery(id+"F6.opExtrude","SWEPT_FACE",FACE,{"disambiguationData":[OSD([sQuery(id+"F5.wireOp",EDGE,"E35.filletArc")])]})])],"derivedFrom":makeQuery(id+"F6.opExtrude","CAP_EDGE",EDGE,{"disambiguationData":[OSD([subQ0])],"isStart":false})});}
            var Q4;
            {var subQ0=sQuery(id+"F0.wireOp",EDGE,"E25.7");var subQ1=sQuery(id+"F0.wireOp",EDGE,"E25.6");var subQ2=sQuery(id+"F0.wireOp",EDGE,"E25.5");var subQ3=sQuery(id+"F0.wireOp",EDGE,"E25.4");var subQ4=sQuery(id+"F0.wireOp",EDGE,"E25.0");var subQ5=sQuery(id+"F0.wireOp",EDGE,"E25.1");var subQ6=sQuery(id+"F0.wireOp",EDGE,"E25.2");var subQ7=sQuery(id+"F0.wireOp",EDGE,"E25.3");Q4=makeQuery(id+"F9.boolean.opBoolean","INTERSECT",EDGE,{"derivedFrom":[makeQuery(id+"F6.boolean.opBoolean","SPLIT",FACE,{"disambiguationData":[TD([makeQuery(id+"F2.opExtrude","SWEPT_FACE",FACE,{"disambiguationData":[OSD([subQ4])]})])],"derivedFrom":makeQuery(id+"F4.boolean.opBoolean","COPY",FACE,{"derivedFrom":makeQuery(id+"F4.opExtrude","CAP_FACE",FACE,{"disambiguationData":[OSD([subQ4,subQ5,subQ6,subQ7,subQ3,subQ2,subQ1,subQ0])],"isStart":false})})}),makeQuery(id+"F9.opExtrude","SWEPT_FACE",FACE,{"disambiguationData":[OSD([sQuery(id+"F8.wireOp",EDGE,"E67")])]})]});}
            var Q5;
            Q5=makeQuery(id+"F9.boolean.opBoolean","INTERSECT",EDGE,{"disambiguationData":[OD(0.0)],"derivedFrom":[makeQuery(id+"F6.opExtrude","SWEPT_FACE",FACE,{"disambiguationData":[OSD([sQuery(id+"F5.wireOp",EDGE,"E30")])]}),makeQuery(id+"F9.opExtrude","SWEPT_FACE",FACE,{"disambiguationData":[OSD([sQuery(id+"F8.wireOp",EDGE,"E67")])]})]});
            fillet(context, id + "F15", {"entities" : qUnion([Q0, Q1, Q2, Q3, Q4, Q5]), "radius" : 3 * mm, "tangentPropagation" : true, "allowEdgeOverflow" : false});
        }
        {
            var Q0;
            Q0=makeQuery(id+"F1.opExtrude","CAP_EDGE",EDGE,{"disambiguationData":[OSD([sQuery(id+"F0.wireOp",EDGE,"E1.bottom")])],"isStart":false});
            fillet(context, id + "F16", {"entities" : qUnion([Q0]), "radius" : 2 * mm, "tangentPropagation" : true, "allowEdgeOverflow" : false});
        }
        {
            var Q0;
            {var subQ0=sQuery(id+"F0.wireOp",EDGE,"E21.filletArc");var subQ1=sQuery(id+"F0.wireOp",EDGE,"E7");var subQ2=sQuery(id+"F0.wireOp",EDGE,"E6");var subQ3=sQuery(id+"F0.wireOp",EDGE,"E5");var subQ4=sQuery(id+"F0.wireOp",EDGE,"E4");var subQ5=sQuery(id+"F0.wireOp",EDGE,"E22.filletArc");var subQ6=sQuery(id+"F0.wireOp",EDGE,"E1.bottom");var subQ7=sQuery(id+"F0.wireOp",EDGE,"E1.right");var subQ8=sQuery(id+"F0.wireOp",EDGE,"E1.top");var subQ9=sQuery(id+"F0.wireOp",EDGE,"E1.left");var subQ10=sQuery(id+"F0.wireOp",EDGE,"E23.filletArc");var subQ11=sQuery(id+"F0.wireOp",EDGE,"E24.filletArc");Q0=makeQuery(id+"F2.boolean.opBoolean","SPLIT",FACE,{"disambiguationData":[TD([makeQuery(id+"F1.opExtrude","SWEPT_FACE",FACE,{"disambiguationData":[OSD([subQ6])]})])],"derivedFrom":makeQuery(id+"F1.opExtrude","CAP_FACE",FACE,{"disambiguationData":[OSD([subQ6,subQ8,subQ9,subQ7,subQ4,subQ3,subQ2,subQ1,subQ0,subQ5,subQ10,subQ11])],"isStart":true})});}
            var Q1;
            Q1 = qSketchRegion(id + "F0", true);
            extrude(context, id + "F17", {"entities" : qUnion([Q0, Q1]), "operationType" : NewBodyOperationType.ADD, "depth" : 25 * mm});
        }
        {
            var Q0;
            Q0=makeQuery(id+"F17.opExtrude","CAP_FACE",FACE,{"disambiguationData":[OSD([sQuery(id+"F0.wireOp",EDGE,"E1.bottom"),sQuery(id+"F0.wireOp",EDGE,"E1.top"),sQuery(id+"F0.wireOp",EDGE,"E1.left"),sQuery(id+"F0.wireOp",EDGE,"E1.right"),sQuery(id+"F0.wireOp",EDGE,"E4"),sQuery(id+"F0.wireOp",EDGE,"E5"),sQuery(id+"F0.wireOp",EDGE,"E6"),sQuery(id+"F0.wireOp",EDGE,"E7"),sQuery(id+"F0.wireOp",EDGE,"E21.filletArc"),sQuery(id+"F0.wireOp",EDGE,"E22.filletArc"),sQuery(id+"F0.wireOp",EDGE,"E23.filletArc"),sQuery(id+"F0.wireOp",EDGE,"E24.filletArc"),sQuery(id+"F0.wireOp",EDGE,"E26.0"),sQuery(id+"F0.wireOp",EDGE,"E26.1"),sQuery(id+"F0.wireOp",EDGE,"E26.2"),sQuery(id+"F0.wireOp",EDGE,"E26.3"),sQuery(id+"F0.wireOp",EDGE,"E26.4"),sQuery(id+"F0.wireOp",EDGE,"E26.5"),sQuery(id+"F0.wireOp",EDGE,"E26.6"),sQuery(id+"F0.wireOp",EDGE,"E26.7")])],"isStart":false});
            var sketch = newSketch(context, id + "F18", { "sketchPlane" : qUnion([Q0])});
            skLineSegment(sketch, "E79.0", {"start": v(-70, 90) * mm, "end": v(70, 90) * mm});
            skArc(sketch, "E79.1", {"start": v(-70, 90) * mm, "mid": v(-77.07, 87.07) * mm, "end": v(-80, 80) * mm});
            skLineSegment(sketch, "E79.2", {"start": v(-80, -80) * mm, "end": v(-80, 80) * mm});
            skCircle(sketch, "E79.3", {"center": v(-60, 67.5) * mm, "radius": 4 * mm});
            skArc(sketch, "E79.4", {"start": v(58.62, 51.33) * mm, "mid": v(0, 71.5) * mm, "end": v(-58.62, 51.33) * mm});
            skArc(sketch, "E79.5", {"start": v(-58.62, 51.33) * mm, "mid": v(-62.58, 46.43) * mm, "end": v(-64, 40.3) * mm});
            skLineSegment(sketch, "E79.6", {"start": v(-64, 40.3) * mm, "end": v(-64, -40.3) * mm});
            skArc(sketch, "E79.7", {"start": v(-64, -40.3) * mm, "mid": v(-62.58, -46.43) * mm, "end": v(-58.62, -51.33) * mm});
            skCircle(sketch, "E79.8", {"center": v(60, 67.5) * mm, "radius": 4 * mm});
            skArc(sketch, "E79.9", {"start": v(80, 80) * mm, "mid": v(77.07, 87.07) * mm, "end": v(70, 90) * mm});
            skLineSegment(sketch, "E79.10", {"start": v(80, -80) * mm, "end": v(80, 80) * mm});
            skArc(sketch, "E79.11", {"start": v(64, 40.3) * mm, "mid": v(62.58, 46.43) * mm, "end": v(58.62, 51.33) * mm});
            skLineSegment(sketch, "E79.12", {"start": v(64, 40.3) * mm, "end": v(64, -40.3) * mm});
            skArc(sketch, "E79.13", {"start": v(58.62, -51.33) * mm, "mid": v(62.58, -46.43) * mm, "end": v(64, -40.3) * mm});
            skArc(sketch, "E79.14", {"start": v(-58.62, -51.33) * mm, "mid": v(0, -71.5) * mm, "end": v(58.62, -51.33) * mm});
            skCircle(sketch, "E79.15", {"center": v(-60, -67.5) * mm, "radius": 4 * mm});
            skArc(sketch, "E79.16", {"start": v(-80, -80) * mm, "mid": v(-77.07, -87.07) * mm, "end": v(-70, -90) * mm});
            skLineSegment(sketch, "E79.17", {"start": v(-70, -90) * mm, "end": v(70, -90) * mm});
            skArc(sketch, "E79.18", {"start": v(70, -90) * mm, "mid": v(77.07, -87.07) * mm, "end": v(80, -80) * mm});
            skCircle(sketch, "E79.19", {"center": v(60, -67.5) * mm, "radius": 4 * mm});
            skLineSegment(sketch, "E80", {"start": v(0, 90) * mm, "end": v(0, 120) * mm, "construction": true});
            skPoint(sketch, "E80.endSnap0", {"position": v(0, 90) * mm});
            skLineSegment(sketch, "E81", {"start": v(-33, 90) * mm, "end": v(-15, 108) * mm});
            skLineSegment(sketch, "E82", {"start": v(-15, 108) * mm, "end": v(-15, 120) * mm});
            skArc(sketch, "E83", {"start": v(-15, 120) * mm, "mid": v(0, 135) * mm, "end": v(15, 120) * mm});
            skLineSegment(sketch, "E84", {"start": v(15, 120) * mm, "end": v(15, 108) * mm});
            skLineSegment(sketch, "E85", {"start": v(15, 108) * mm, "end": v(33, 90) * mm});
            skCircle(sketch, "E86", {"center": v(0, 120) * mm, "radius": 6 * mm});
            skLineSegment(sketch, "E87", {"start": v(-80, 0) * mm, "end": v(80, 0) * mm, "construction": true});
            skLineSegment(sketch, "E88.MirrorCS", {"start": v(-33, -90) * mm, "end": v(-15, -108) * mm});
            skLineSegment(sketch, "E89.MirrorCS", {"start": v(-15, -108) * mm, "end": v(-15, -120) * mm});
            skArc(sketch, "E90.MirrorCS", {"start": v(-15, -120) * mm, "mid": v(0, -135) * mm, "end": v(15, -120) * mm});
            skLineSegment(sketch, "E91.MirrorCS", {"start": v(15, -120) * mm, "end": v(15, -108) * mm});
            skLineSegment(sketch, "E92.MirrorCS", {"start": v(15, -108) * mm, "end": v(33, -90) * mm});
            skLineSegment(sketch, "E93.MirrorCS", {"start": v(0, -90) * mm, "end": v(0, -120) * mm, "construction": true});
            skCircle(sketch, "E94.MirrorC", {"center": v(0, -120) * mm, "radius": 6 * mm});
            skSolve(sketch);
        }
        {
            var Q0;
            Q0 = qSketchRegion(id + "F18", true);
            extrude(context, id + "F19", {"entities" : qUnion([Q0]), "operationType" : NewBodyOperationType.ADD, "depth" : 25 * mm, "offsetDistance" : 25 * mm});
        }
    });
